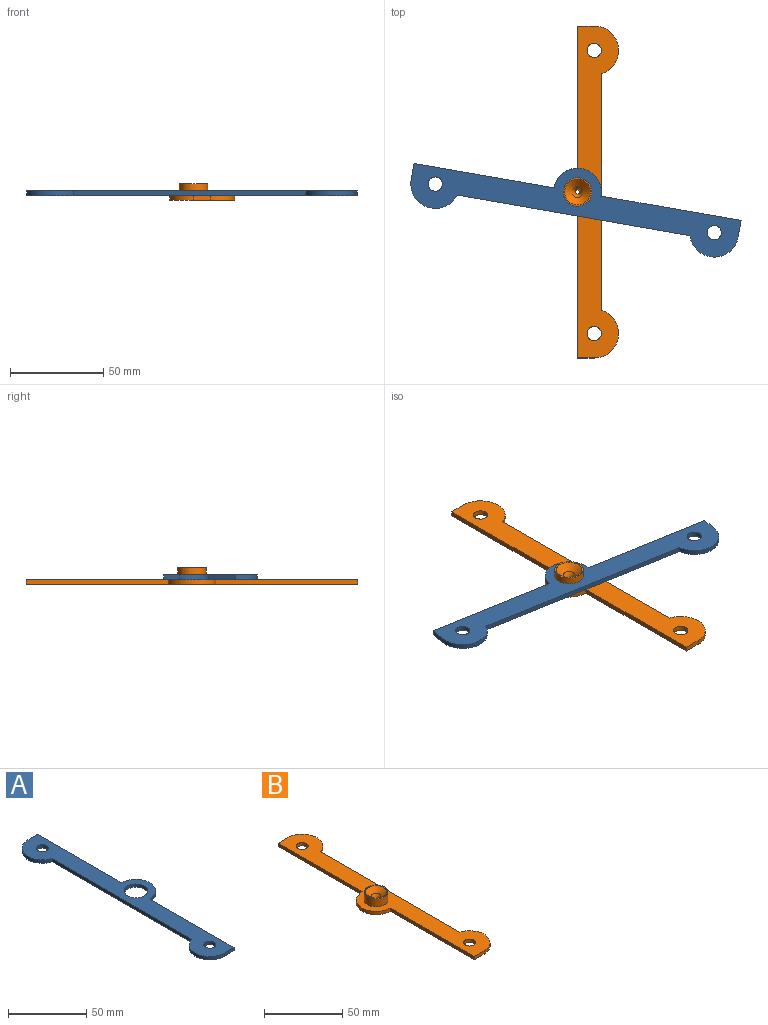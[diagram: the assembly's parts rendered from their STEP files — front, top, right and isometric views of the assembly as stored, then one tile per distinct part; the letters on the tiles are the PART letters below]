
ASSEMBLY  parts=2 mates=1
PART A: 13 faces, bbox 34.7x177.8x2.5 mm
  f0: cylinder r=3.81mm len=7.62mm, axis (0,0,-1), area 60.8mm2, adj f9,f11
  f1: cylinder r=3.81mm len=7.62mm, axis (0,0,-1), area 60.8mm2, adj f9,f11
  f2: plane 76.2x2.54mm, normal (1,0,0), area 193.5mm2, adj f3,f9,f10,f11
  f3: plane 8.89x2.54mm, normal (0,-1,0), area 22.6mm2, adj f2,f4,f9,f11
  f4: cylinder r=13.09mm len=25.62mm, axis (0,0,-1), area 94.7mm2, adj f3,f5,f9,f11
  f5: plane 126.56x2.54mm, normal (-1,0,0), area 321.5mm2, adj f4,f6,f9,f11
  f6: cylinder r=13.09mm len=25.62mm, axis (0,0,-1), area 94.7mm2, adj f5,f7,f9,f11
  f7: plane 8.89x2.54mm, normal (0,1,0), area 22.6mm2, adj f6,f8,f9,f11
  f8: plane 76.2x2.54mm, normal (1,0,0), area 193.5mm2, adj f7,f9,f10,f11
  f9: plane 177.8x34.68mm, normal (0,0,1), area 2578.2mm2, adj f0,f1,f2,f3,f4,f5,f6,f7
  f10: cylinder r=12.7mm len=25.4mm, axis (0,0,-1), area 101.3mm2, adj f2,f8,f9,f11
  f11: plane 177.8x34.68mm, normal (0,0,-1), area 2578.2mm2, adj f0,f1,f2,f3,f4,f5,f6,f7
  f12: cylinder r=7.62mm len=15.24mm, axis (0,0,1), area 121.6mm2, adj f9,f11
PART B: 17 faces, bbox 34.7x177.8x8.9 mm
  f0: plane 76.2x2.54mm, normal (-1,0,0), area 193.5mm2, adj f4,f5,f6,f11
  f1: plane 126.56x2.54mm, normal (1,0,0), area 321.5mm2, adj f2,f5,f6,f8
  f2: cylinder r=13.09mm len=25.62mm, axis (0,0,-1), area 94.7mm2, adj f1,f4,f5,f6
  f3: cylinder r=3.81mm len=7.62mm, axis (0,0,-1), area 60.8mm2, adj f5,f6
  f4: plane 8.89x2.54mm, normal (0,1,0), area 22.6mm2, adj f0,f2,f5,f6
  f5: plane 177.8x34.68mm, normal (0,0,1), area 2578.2mm2, adj f0,f1,f2,f3,f4,f7,f8,f9
  f6: plane 177.8x34.68mm, normal (0,0,-1), area 2755.6mm2, adj f0,f1,f2,f3,f4,f7,f8,f9
  f7: plane 76.2x2.54mm, normal (-1,0,0), area 193.5mm2, adj f5,f6,f10,f11
  f8: cylinder r=13.09mm len=25.62mm, axis (0,0,-1), area 94.7mm2, adj f1,f5,f6,f10
  f9: cylinder r=3.81mm len=7.62mm, axis (0,0,-1), area 60.8mm2, adj f5,f6
  f10: plane 8.89x2.54mm, normal (0,-1,0), area 22.6mm2, adj f5,f6,f7,f8
  f11: cylinder r=12.7mm len=25.4mm, axis (0,0,-1), area 101.3mm2, adj f0,f5,f6,f7
  f12: cylinder r=1.27mm len=2.54mm, axis (0,0,-1), area 10.5mm2, adj f6,f16
  f13: cylinder r=7.62mm len=15.24mm, axis (0,0,-1), area 304mm2, adj f5,f14
  f14: plane 15.24x15.24mm, normal (0,0,1), area 32.3mm2, adj f13,f15
  f15: cone r=1.27mm half-angle=48deg, axis (0,0,1), area 160.8mm2, adj f14,f16
  f16: torus R=6.86mm, axis (0,0,-1), area 55.9mm2, adj f12,f15
PLACE A rot(axis=(0,0,1),80.1deg) t=(-19.99,-63.84,5.95)mm
PLACE B t=(-11.71,-16.29,3.41)mm fixed
MATE revolute A.f10 <-> B.f11  axis (0,0,-1) through (-11.71,-16.29,5.95)mm
